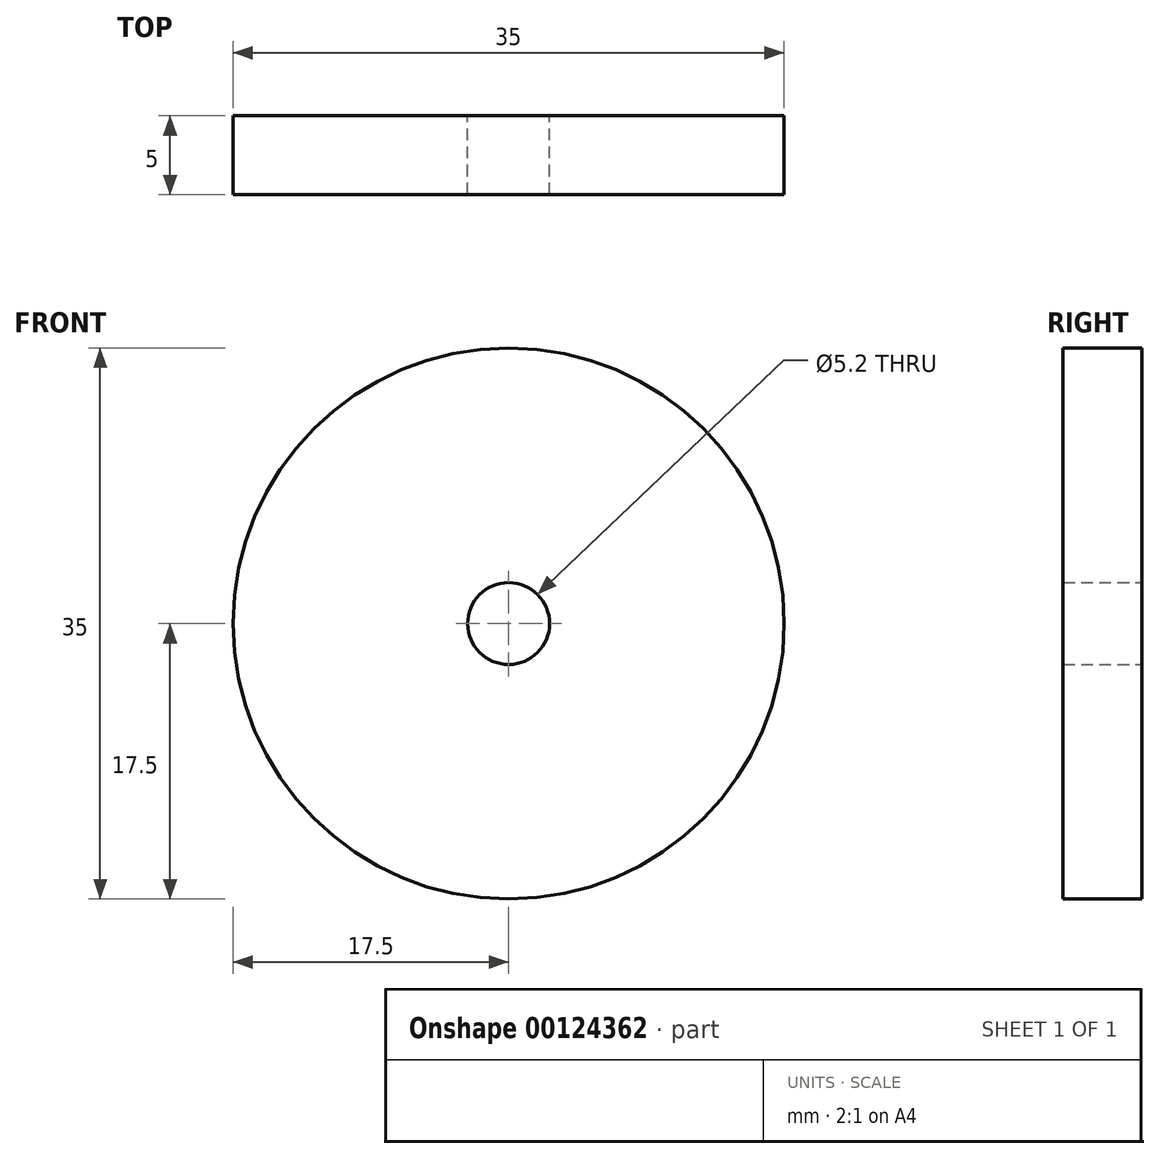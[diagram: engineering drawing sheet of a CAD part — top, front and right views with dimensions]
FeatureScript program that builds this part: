
annotation { "Feature Type Name" : "Feature", "Feature Type Description" : "" }
export const myFeature = defineFeature(function(context is Context, id is Id, definition is map)
    precondition{}
    {
        {
            var Q0;
            Q0=qCreatedBy(makeId("Front.planeOp"),FACE);
            var sketch = newSketch(context, id + "F0", { "sketchPlane" : qUnion([Q0])});
            skCircle(sketch, "E0", {"center": v(0, 0) * mm, "radius": 2.6 * mm});
            skCircle(sketch, "E1", {"center": v(0, 0) * mm, "radius": 17.5 * mm});
            skSolve(sketch);
        }
        {
            var Q0;
            Q0=makeQuery(id+"F0.imprint","IMPRINT",FACE,{"disambiguationData":[TD([[makeQuery(id+"F0.imprint","IMPRINT",EDGE,{"derivedFrom":sQuery(id+"F0.wireOp",EDGE,"E0")}),-1.0]])]});
            extrude(context, id + "F1", {"entities" : qUnion([Q0]), "depth" : 5 * mm});
        }
    });
